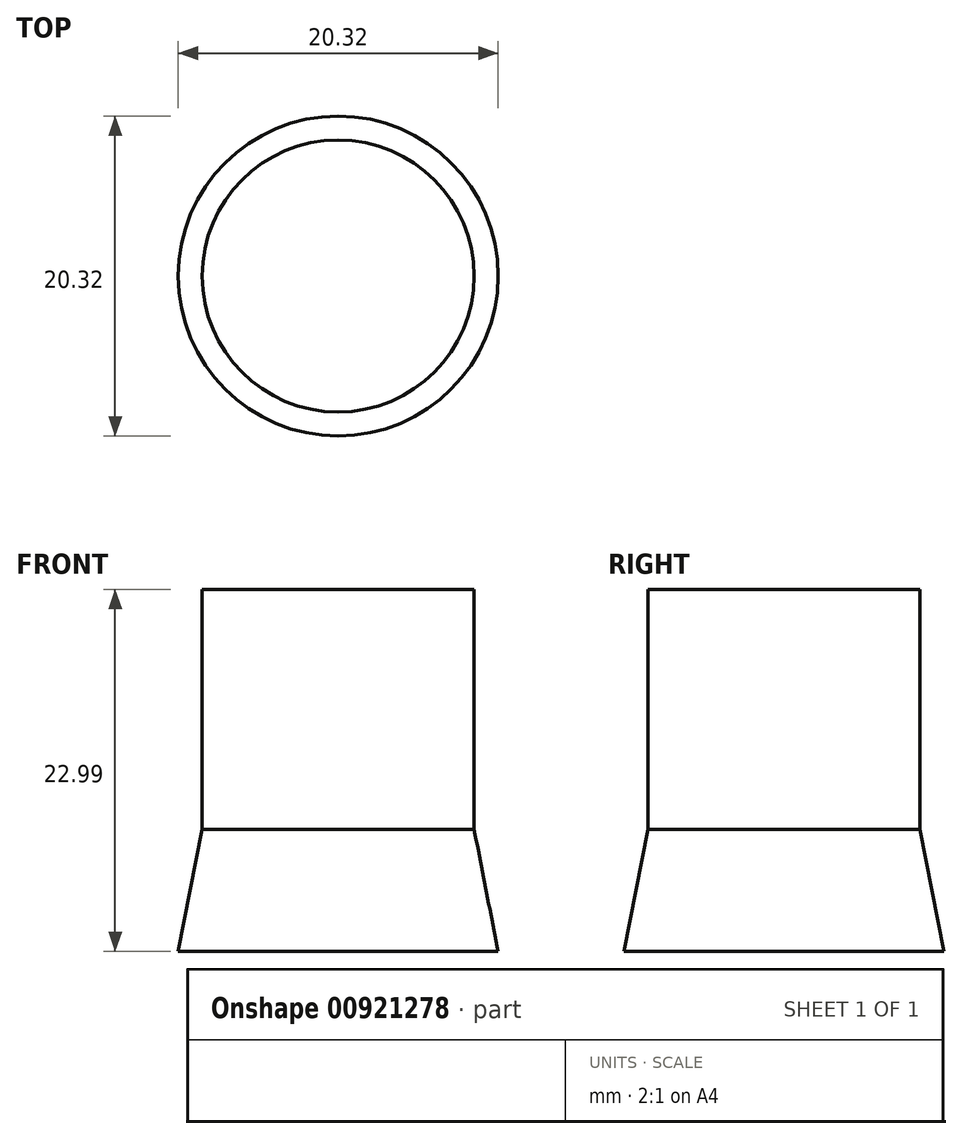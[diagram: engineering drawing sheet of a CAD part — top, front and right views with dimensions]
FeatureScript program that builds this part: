
annotation { "Feature Type Name" : "Feature", "Feature Type Description" : "" }
export const myFeature = defineFeature(function(context is Context, id is Id, definition is map)
    precondition{}
    {
        {
            var Q0;
            Q0=qCreatedBy(makeId("Front.planeOp"),FACE);
            var sketch = newSketch(context, id + "F0", { "sketchPlane" : qUnion([Q0])});
            skLineSegment(sketch, "E0", {"start": v(-8.64, 15.24) * mm, "end": v(-8.64, 0) * mm});
            skLineSegment(sketch, "E1", {"start": v(-8.64, 0) * mm, "end": v(-10.16, -7.75) * mm});
            skLineSegment(sketch, "E2", {"start": v(-10.16, -7.75) * mm, "end": v(0, -7.75) * mm});
            skLineSegment(sketch, "E3", {"start": v(0, -7.75) * mm, "end": v(0, 15.24) * mm});
            skLineSegment(sketch, "E4", {"start": v(0, 15.24) * mm, "end": v(-8.64, 15.24) * mm});
            skSolve(sketch);
        }
        {
            var Q0;
            Q0=makeQuery(id+"F0.imprint","IMPRINT",FACE,{"disambiguationData":[TD([[makeQuery(id+"F0.imprint","IMPRINT",EDGE,{"derivedFrom":sQuery(id+"F0.wireOp",EDGE,"E0")}),1.0]])]});
            var Q1;
            Q1=sQuery(id+"F0.wireOp",EDGE,"E3");
            revolve(context, id + "F1", {"surfaceOperationType" : NewSurfaceOperationType.NEW, "entities" : qUnion([Q0]), "axis" : qUnion([Q1]), "revolveType" : RevolveType.FULL, "oppositeDirection" : true});
        }
    });
